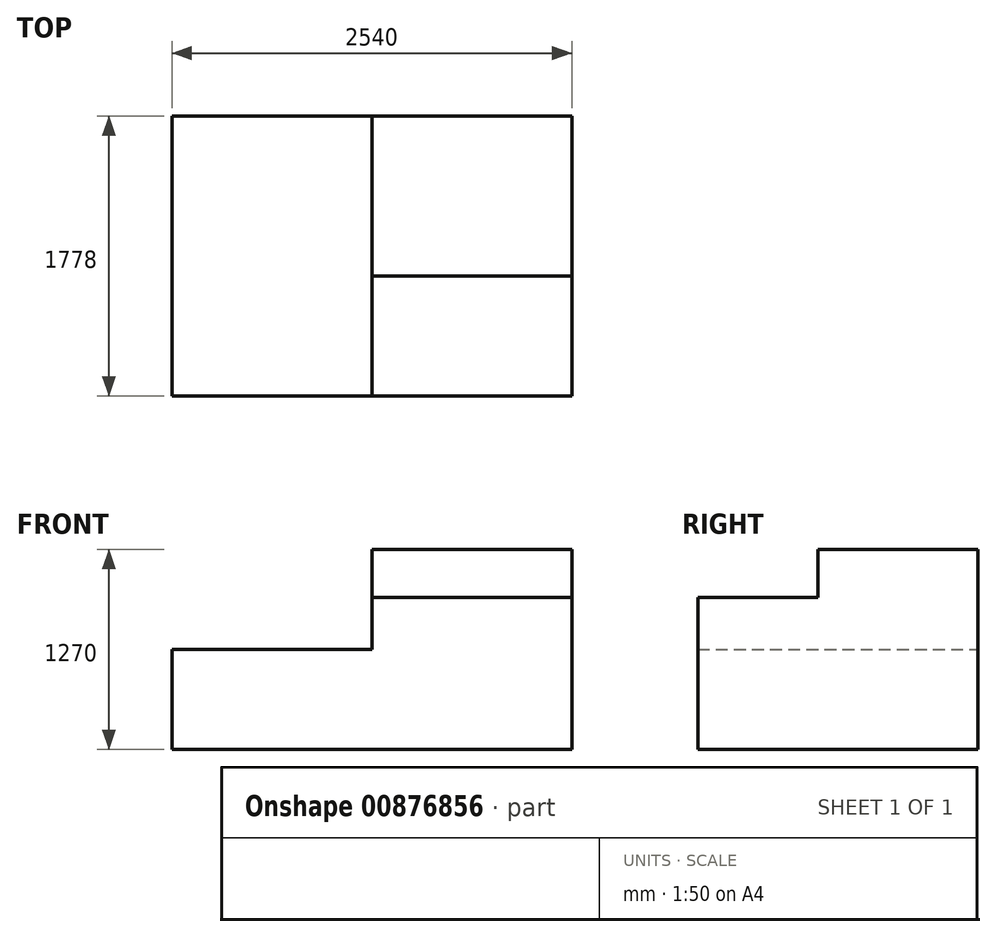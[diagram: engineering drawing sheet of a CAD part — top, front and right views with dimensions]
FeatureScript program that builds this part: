
annotation { "Feature Type Name" : "Feature", "Feature Type Description" : "" }
export const myFeature = defineFeature(function(context is Context, id is Id, definition is map)
    precondition{}
    {
        {
            var Q0;
            Q0=qCreatedBy(makeId("Top.planeOp"),FACE);
            var sketch = newSketch(context, id + "F0", { "sketchPlane" : qUnion([Q0])});
            skLineSegment(sketch, "E0.bottom", {"start": v(635, -889) * mm, "end": v(-635, -889) * mm});
            skLineSegment(sketch, "E0.top", {"start": v(635, 889) * mm, "end": v(-635, 889) * mm});
            skLineSegment(sketch, "E0.left", {"start": v(635, -889) * mm, "end": v(635, 889) * mm});
            skLineSegment(sketch, "E0.right", {"start": v(-635, -889) * mm, "end": v(-635, 889) * mm});
            skPoint(sketch, "E0.middle", {"position": v(0, 0) * mm});
            skLineSegment(sketch, "E1.bottom", {"start": v(635, -889) * mm, "end": v(1905, -889) * mm});
            skLineSegment(sketch, "E1.top", {"start": v(635, -127) * mm, "end": v(1905, -127) * mm});
            skLineSegment(sketch, "E1.left", {"start": v(635, -889) * mm, "end": v(635, -127) * mm});
            skLineSegment(sketch, "E1.right", {"start": v(1905, -889) * mm, "end": v(1905, -127) * mm});
            skLineSegment(sketch, "E2.bottom", {"start": v(635, 889) * mm, "end": v(1905, 889) * mm});
            skLineSegment(sketch, "E2.left", {"start": v(635, 889) * mm, "end": v(635, -127) * mm});
            skLineSegment(sketch, "E2.right", {"start": v(1905, 889) * mm, "end": v(1905, -127) * mm});
            skSolve(sketch);
        }
        {
            var Q0;
            Q0=makeQuery(id+"F0.imprint","IMPRINT",FACE,{"disambiguationData":[TD([[makeQuery(id+"F0.imprint","IMPRINT",EDGE,{"derivedFrom":sQuery(id+"F0.wireOp",EDGE,"E0.bottom")}),-1.0]])]});
            extrude(context, id + "F1", {"entities" : qUnion([Q0]), "depth" : 635 * mm, "offsetDistance" : 25.4 * mm});
        }
        {
            var Q0;
            Q0=makeQuery(id+"F0.imprint","IMPRINT",FACE,{"disambiguationData":[TD([[makeQuery(id+"F0.imprint","IMPRINT",EDGE,{"derivedFrom":sQuery(id+"F0.wireOp",EDGE,"E1.bottom")}),1.0]])]});
            var sketch = newSketch(context, id + "F2", { "sketchPlane" : qUnion([Q0])});
            skSolve(sketch);
        }
        {
            var Q0;
            Q0 = qSketchRegion(id + "F2", true);
            var Q1;
            Q1=makeQuery(id+"F0.imprint","IMPRINT",FACE,{"disambiguationData":[TD([[makeQuery(id+"F0.imprint","IMPRINT",EDGE,{"derivedFrom":sQuery(id+"F0.wireOp",EDGE,"E1.bottom")}),1.0]])]});
            extrude(context, id + "F3", {"entities" : qUnion([Q0, Q1]), "operationType" : NewBodyOperationType.ADD, "depth" : 965.2 * mm, "offsetDistance" : 25.4 * mm});
        }
        {
            var Q0;
            Q0=makeQuery(id+"F0.imprint","IMPRINT",FACE,{"disambiguationData":[TD([[makeQuery(id+"F0.imprint","IMPRINT",EDGE,{"derivedFrom":sQuery(id+"F0.wireOp",EDGE,"E2.bottom")}),-1.0]])]});
            extrude(context, id + "F4", {"entities" : qUnion([Q0]), "operationType" : NewBodyOperationType.ADD, "depth" : 1270 * mm, "offsetDistance" : 25.4 * mm});
        }
    });
